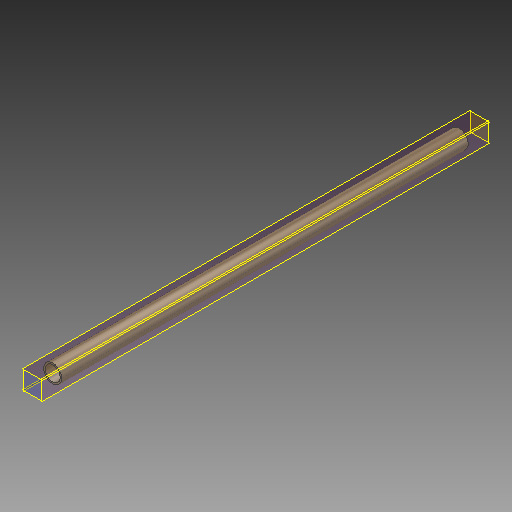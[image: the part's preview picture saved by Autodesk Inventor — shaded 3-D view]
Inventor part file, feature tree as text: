
AUTODESK INVENTOR PART (.ipt)
format: ipt  version: 2018 (Build 220112000, 112)  size: 98,304 bytes
history: native  units: mm
features: other x5, extrude x1, sketch x1
ambient origin geometry x8: Origin, YZ Plane, XZ Plane, XY Plane, X Axis, Y Axis, Z Axis, Center Point
bodies: Body1 (feature_tree)
feature tree (7):
  other  "ソリッド1"
  extrude  "押し出し1"  Depth=27.2mm
  other  "作業平面1"
  other  "作業平面2"
  other  "作業平面3"
  other  "作業平面4"
  sketch  "スケッチ1"
